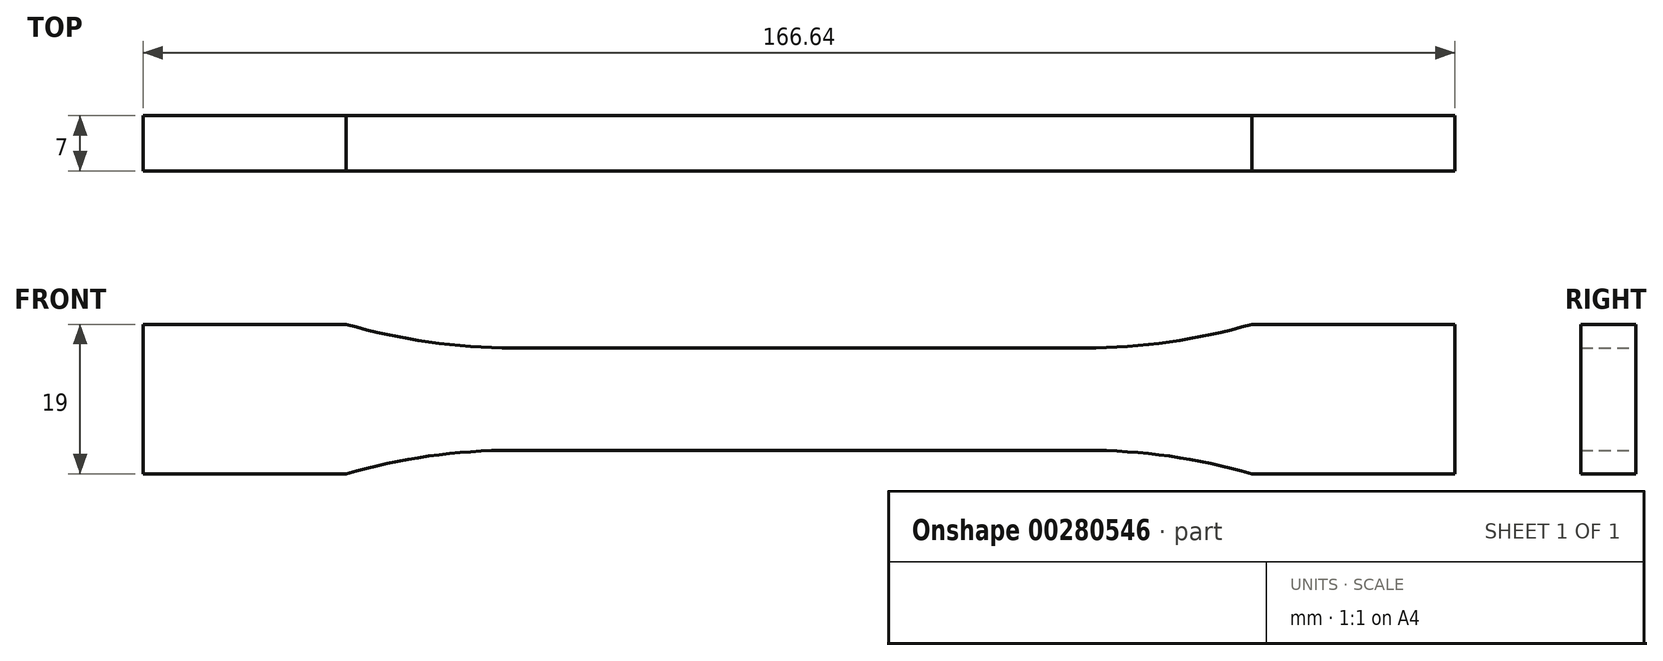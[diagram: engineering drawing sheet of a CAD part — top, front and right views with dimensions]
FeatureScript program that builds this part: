
annotation { "Feature Type Name" : "Feature", "Feature Type Description" : "" }
export const myFeature = defineFeature(function(context is Context, id is Id, definition is map)
    precondition{}
    {
        {
            var Q0;
            Q0=qCreatedBy(makeId("Front.planeOp"),FACE);
            var sketch = newSketch(context, id + "F0", { "sketchPlane" : qUnion([Q0])});
            skLineSegment(sketch, "E0", {"start": v(0, 6.5) * mm, "end": v(36.36, 6.5) * mm});
            skArc(sketch, "E1", {"start": v(36.36, 6.5) * mm, "mid": v(47.04, 7.25) * mm, "end": v(57.5, 9.5) * mm});
            skLineSegment(sketch, "E2", {"start": v(57.5, 9.5) * mm, "end": v(83.32, 9.5) * mm});
            skLineSegment(sketch, "E3.MirrorCS", {"start": v(57.5, -9.5) * mm, "end": v(83.32, -9.5) * mm});
            skLineSegment(sketch, "E4.MirrorCS", {"start": v(0, -6.5) * mm, "end": v(36.36, -6.5) * mm});
            skArc(sketch, "E5.MirrorCS", {"start": v(36.36, -6.5) * mm, "mid": v(47.04, -7.25) * mm, "end": v(57.5, -9.5) * mm});
            skArc(sketch, "E6.MirrorCS", {"start": v(-36.36, -6.5) * mm, "mid": v(-47.04, -7.25) * mm, "end": v(-57.5, -9.5) * mm});
            skLineSegment(sketch, "E7.MirrorCS", {"start": v(0, 6.5) * mm, "end": v(-36.36, 6.5) * mm});
            skArc(sketch, "E8.MirrorCS", {"start": v(-36.36, 6.5) * mm, "mid": v(-47.04, 7.25) * mm, "end": v(-57.5, 9.5) * mm});
            skLineSegment(sketch, "E9.MirrorCS", {"start": v(-57.5, -9.5) * mm, "end": v(-83.32, -9.5) * mm});
            skLineSegment(sketch, "E10.MirrorCS", {"start": v(0, -6.5) * mm, "end": v(-36.36, -6.5) * mm});
            skLineSegment(sketch, "E11.MirrorCS", {"start": v(-57.5, 9.5) * mm, "end": v(-83.32, 9.5) * mm});
            skLineSegment(sketch, "E12", {"start": v(-83.32, 9.5) * mm, "end": v(-83.32, -9.5) * mm});
            skLineSegment(sketch, "E13", {"start": v(83.32, 9.5) * mm, "end": v(83.32, -9.5) * mm});
            skSolve(sketch);
        }
        {
            var Q0;
            Q0=makeQuery(id+"F0.imprint","IMPRINT",FACE,{"disambiguationData":[TD([[makeQuery(id+"F0.imprint","IMPRINT",EDGE,{"derivedFrom":sQuery(id+"F0.wireOp",EDGE,"E0")}),-1.0]])]});
            extrude(context, id + "F1", {"entities" : qUnion([Q0]), "endBound" : BoundingType.SYMMETRIC, "depth" : 7 * mm});
        }
    });
